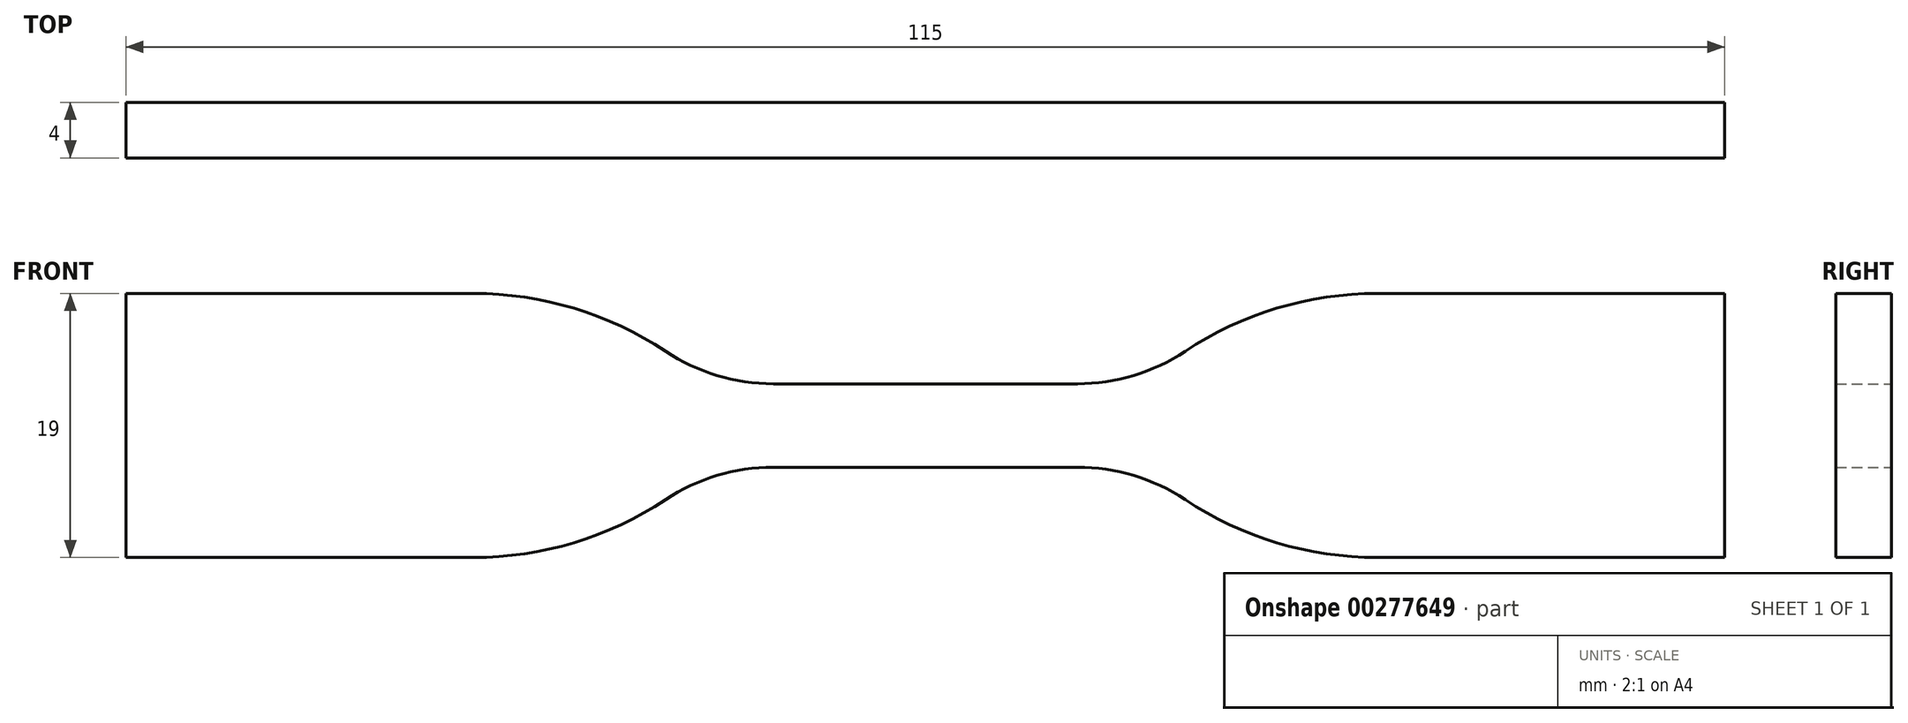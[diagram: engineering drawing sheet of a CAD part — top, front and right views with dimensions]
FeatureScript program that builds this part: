
annotation { "Feature Type Name" : "Feature", "Feature Type Description" : "" }
export const myFeature = defineFeature(function(context is Context, id is Id, definition is map)
    precondition{}
    {
        {
            var Q0;
            Q0=qCreatedBy(makeId("Front.planeOp"),FACE);
            var sketch = newSketch(context, id + "F0", { "sketchPlane" : qUnion([Q0])});
            skLineSegment(sketch, "E0", {"start": v(0, 3) * mm, "end": v(10.94, 3) * mm});
            skLineSegment(sketch, "E1", {"start": v(32.5, 9.5) * mm, "end": v(57.5, 9.5) * mm});
            skLineSegment(sketch, "E2.MirrorCS", {"start": v(0, -3) * mm, "end": v(10.94, -3) * mm});
            skLineSegment(sketch, "E3.MirrorCS", {"start": v(32.5, -9.5) * mm, "end": v(57.5, -9.5) * mm});
            skLineSegment(sketch, "E4.MirrorCS", {"start": v(0, 3) * mm, "end": v(-10.94, 3) * mm});
            skLineSegment(sketch, "E5.MirrorCS", {"start": v(-32.5, -9.5) * mm, "end": v(-57.5, -9.5) * mm});
            skLineSegment(sketch, "E6.MirrorCS", {"start": v(-32.5, 9.5) * mm, "end": v(-57.5, 9.5) * mm});
            skLineSegment(sketch, "E7.MirrorCS", {"start": v(0, -3) * mm, "end": v(-10.94, -3) * mm});
            skLineSegment(sketch, "E8", {"start": v(-57.5, 9.5) * mm, "end": v(-57.5, -9.5) * mm});
            skLineSegment(sketch, "E9", {"start": v(57.5, 9.5) * mm, "end": v(57.5, -9.5) * mm});
            skArc(sketch, "E10", {"start": v(-18.68, 5.33) * mm, "mid": v(-25.28, 8.44) * mm, "end": v(-32.5, 9.5) * mm});
            skArc(sketch, "E11", {"start": v(32.5, 9.5) * mm, "mid": v(25.28, 8.44) * mm, "end": v(18.68, 5.33) * mm});
            skArc(sketch, "E12", {"start": v(-32.5, -9.5) * mm, "mid": v(-25.28, -8.44) * mm, "end": v(-18.68, -5.33) * mm});
            skArc(sketch, "E13", {"start": v(18.68, -5.33) * mm, "mid": v(25.28, -8.44) * mm, "end": v(32.5, -9.5) * mm});
            skPoint(sketch, "E14.visualSharp", {"position": v(-15.68, 3) * mm});
            skArc(sketch, "E14.filletArc", {"start": v(-18.68, 5.33) * mm, "mid": v(-14.98, 3.6) * mm, "end": v(-10.94, 3) * mm});
            skPoint(sketch, "E15.visualSharp", {"position": v(-15.68, -3) * mm});
            skArc(sketch, "E15.filletArc", {"start": v(-10.94, -3) * mm, "mid": v(-14.98, -3.6) * mm, "end": v(-18.68, -5.33) * mm});
            skPoint(sketch, "E16.visualSharp", {"position": v(15.68, 3) * mm});
            skArc(sketch, "E16.filletArc", {"start": v(10.94, 3) * mm, "mid": v(14.98, 3.6) * mm, "end": v(18.68, 5.33) * mm});
            skPoint(sketch, "E17.visualSharp", {"position": v(15.68, -3) * mm});
            skArc(sketch, "E17.filletArc", {"start": v(18.68, -5.33) * mm, "mid": v(14.98, -3.6) * mm, "end": v(10.94, -3) * mm});
            skSolve(sketch);
        }
        {
            var Q0;
            Q0 = qSketchRegion(id + "F0", true);
            extrude(context, id + "F1", {"entities" : qUnion([Q0]), "endBound" : BoundingType.SYMMETRIC, "depth" : 4 * mm});
        }
    });
